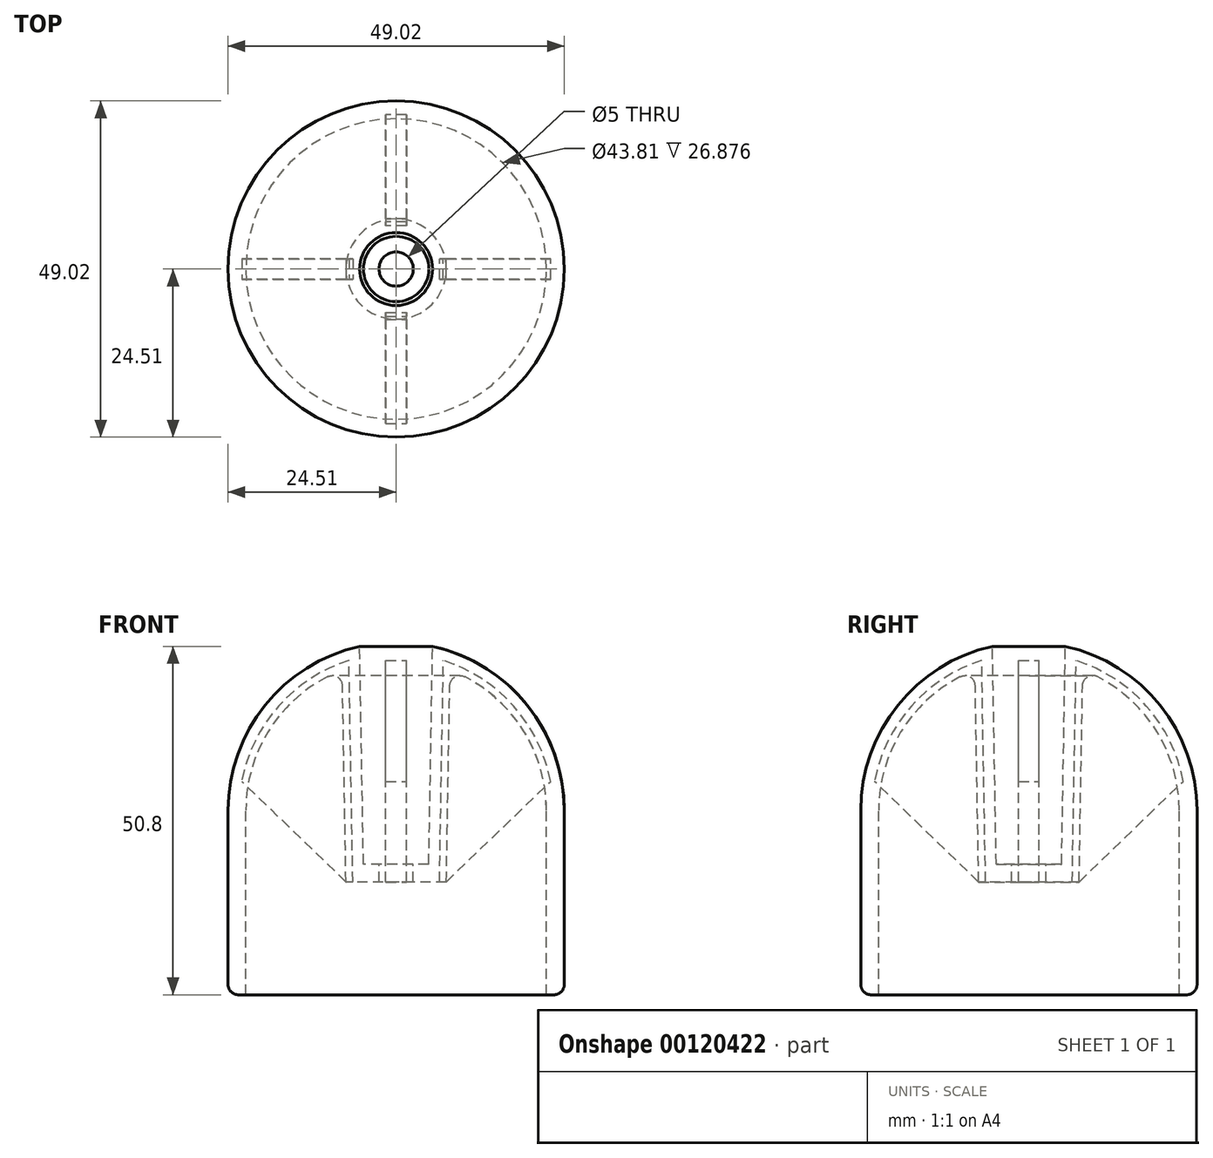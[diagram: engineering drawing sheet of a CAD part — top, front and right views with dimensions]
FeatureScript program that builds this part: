
annotation { "Feature Type Name" : "Feature", "Feature Type Description" : "" }
export const myFeature = defineFeature(function(context is Context, id is Id, definition is map)
    precondition{}
    {
        {
            var Q0;
            Q0=qCreatedBy(makeId("Front.planeOp"),FACE);
            var sketch = newSketch(context, id + "F0", { "sketchPlane" : qUnion([Q0])});
            skLineSegment(sketch, "E0", {"start": v(-21.9, 0) * mm, "end": v(21.9, 0) * mm, "construction": true});
            skLineSegment(sketch, "E1", {"start": v(21.9, 0) * mm, "end": v(24.5, 0) * mm});
            skLineSegment(sketch, "E2", {"start": v(21.9, 0) * mm, "end": v(21.9, 26.88) * mm});
            skArc(sketch, "E3", {"start": v(21.9, 26.88) * mm, "mid": v(18.06, 39.28) * mm, "end": v(7.86, 47.33) * mm});
            skLineSegment(sketch, "E4", {"start": v(0, 48.78) * mm, "end": v(-23.74, 48.78) * mm, "construction": true});
            skArc(sketch, "E5", {"start": v(7.86, 47.33) * mm, "mid": v(4, 48.42) * mm, "end": v(0, 48.78) * mm, "construction": true});
            skLineSegment(sketch, "E6", {"start": v(7.86, 47.33) * mm, "end": v(7.32, 16.45) * mm});
            skLineSegment(sketch, "E7", {"start": v(7.32, 16.45) * mm, "end": v(2.5, 16.45) * mm});
            skLineSegment(sketch, "E8.0", {"start": v(4.76, 19.05) * mm, "end": v(2.5, 19.05) * mm});
            skLineSegment(sketch, "E8.1", {"start": v(5.32, 50.8) * mm, "end": v(4.76, 19.05) * mm});
            skArc(sketch, "E8.2", {"start": v(24.5, 26.88) * mm, "mid": v(19.12, 42.21) * mm, "end": v(5.32, 50.8) * mm});
            skLineSegment(sketch, "E8.3", {"start": v(24.5, 0) * mm, "end": v(24.5, 26.88) * mm});
            skLineSegment(sketch, "E9", {"start": v(2.5, 19.05) * mm, "end": v(2.5, 16.45) * mm});
            skLineSegment(sketch, "E10", {"start": v(4.76, 19.05) * mm, "end": v(-4.76, 19.05) * mm, "construction": true});
            skLineSegment(sketch, "E11", {"start": v(0, 19.05) * mm, "end": v(0, 0) * mm, "construction": true});
            skSolve(sketch);
        }
        {
            var Q0;
            Q0=makeQuery(id+"F0.imprint","IMPRINT",FACE,{"disambiguationData":[TD([[makeQuery(id+"F0.imprint","IMPRINT",EDGE,{"derivedFrom":sQuery(id+"F0.wireOp",EDGE,"E1")}),1.0]])]});
            var Q1;
            Q1=sQuery(id+"F0.wireOp",EDGE,"E11");
            revolve(context, id + "F1", {"entities" : qUnion([Q0]), "axis" : qUnion([Q1]), "revolveType" : RevolveType.FULL});
        }
        {
            var Q0;
            Q0=makeQuery(id+"F1.opRevolve","SWEPT_EDGE",EDGE,{"disambiguationData":[OSD([sQuery(id+"F0.wireOp",EDGE,"E1"),sQuery(id+"F0.wireOp",EDGE,"E8.3")])]});
            fillet(context, id + "F2", {"entities" : qUnion([Q0]), "radius" : 1.5 * mm, "tangentPropagation" : true, "allowEdgeOverflow" : false});
        }
        {
            var Q0;
            Q0=qCreatedBy(makeId("Front.planeOp"),FACE);
            var sketch = newSketch(context, id + "F3", { "sketchPlane" : qUnion([Q0])});
            skArc(sketch, "E12", {"start": v(7.86, 47.33) * mm, "mid": v(18.06, 39.28) * mm, "end": v(21.9, 26.88) * mm, "construction": true});
            skLineSegment(sketch, "E13", {"start": v(21.9, 26.88) * mm, "end": v(21.9, 0) * mm, "construction": true});
            skLineSegment(sketch, "E14", {"start": v(7.32, 16.45) * mm, "end": v(7.86, 47.33) * mm, "construction": true});
            skLineSegment(sketch, "E15", {"start": v(7.32, 16.45) * mm, "end": v(6.32, 16.47) * mm});
            skLineSegment(sketch, "E16", {"start": v(6.32, 16.47) * mm, "end": v(6.88, 48.73) * mm});
            skArc(sketch, "E17.1", {"start": v(6.88, 48.73) * mm, "mid": v(17.13, 42.09) * mm, "end": v(22.51, 31.12) * mm});
            skLineSegment(sketch, "E18", {"start": v(7.32, 16.45) * mm, "end": v(22.51, 31.12) * mm});
            skSolve(sketch);
        }
        {
            var Q0;
            Q0 = qSketchRegion(id + "F3", true);
            extrude(context, id + "F4", {"entities" : qUnion([Q0]), "endBound" : BoundingType.SYMMETRIC, "depth" : 3 * mm});
        }
        {
            var Q0;
            Q0=makeQuery(id+"F4.opExtrude","SWEPT_BODY",BODY,{"disambiguationData":[OSD([sQuery(id+"F3.wireOp",EDGE,"E15"),sQuery(id+"F3.wireOp",EDGE,"E16"),sQuery(id+"F3.wireOp",EDGE,"E17.1"),sQuery(id+"F3.wireOp",EDGE,"E18")])]});
            var Q1;
            Q1=sQuery(id+"F0.wireOp",EDGE,"E11");
            circularPattern(context, id + "F5", {"entities" : qUnion([Q0]), "axis" : qUnion([Q1]), "angle" : 360 * degree, "instanceCount" : 4, "equalSpace" : true});
        }
        {
            var Q0;
            Q0=makeQuery(id+"F1.opRevolve","SWEPT_FACE",FACE,{"disambiguationData":[OSD([sQuery(id+"F0.wireOp",EDGE,"E3")])]});
            fillet(context, id + "F6", {"entities" : qUnion([Q0]), "radius" : 1.5 * mm, "tangentPropagation" : true, "allowEdgeOverflow" : false});
        }
    });
